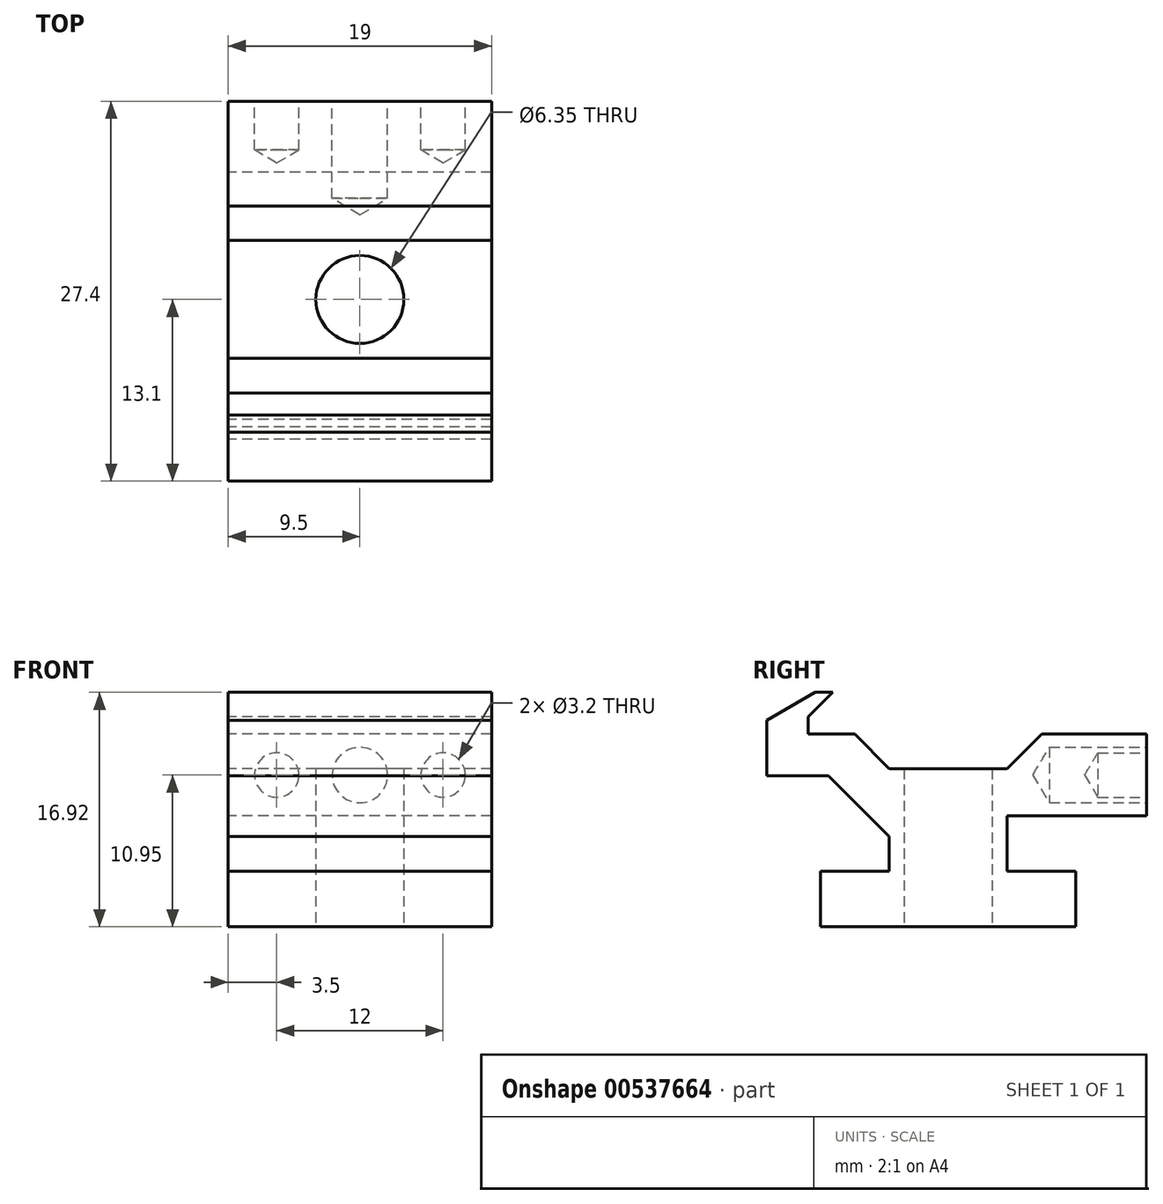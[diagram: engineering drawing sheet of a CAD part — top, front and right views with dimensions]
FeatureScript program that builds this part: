
annotation { "Feature Type Name" : "Feature", "Feature Type Description" : "" }
export const myFeature = defineFeature(function(context is Context, id is Id, definition is map)
    precondition{}
    {
        {
            var Q0;
            Q0=qCreatedBy(makeId("Right.planeOp"),FACE);
            var sketch = newSketch(context, id + "F0", { "sketchPlane" : qUnion([Q0])});
            skLineSegment(sketch, "E0.bottom", {"start": v(-9.2, -8.75) * mm, "end": v(9.2, -8.75) * mm});
            skLineSegment(sketch, "E0.top", {"start": v(-9.2, -4.75) * mm, "end": v(-4.25, -4.75) * mm});
            skLineSegment(sketch, "E0.left", {"start": v(-9.2, -8.75) * mm, "end": v(-9.2, -4.75) * mm});
            skLineSegment(sketch, "E0.right", {"start": v(9.2, -8.75) * mm, "end": v(9.2, -4.75) * mm});
            skLineSegment(sketch, "E1.top", {"start": v(-4.25, 2.65) * mm, "end": v(4.25, 2.65) * mm});
            skLineSegment(sketch, "E1.left", {"start": v(-4.25, -4.75) * mm, "end": v(-4.25, -2.25) * mm});
            skLineSegment(sketch, "E1.right", {"start": v(4.25, -4.75) * mm, "end": v(4.25, -0.75) * mm});
            skLineSegment(sketch, "E2", {"start": v(4.25, 2.65) * mm, "end": v(6.75, 5.15) * mm});
            skLineSegment(sketch, "E3", {"start": v(-4.25, 2.65) * mm, "end": v(-6.75, 5.15) * mm});
            skLineSegment(sketch, "E4", {"start": v(4.25, -0.75) * mm, "end": v(14.3, -0.75) * mm});
            skLineSegment(sketch, "E5", {"start": v(14.3, -0.75) * mm, "end": v(14.3, 5.15) * mm});
            skLineSegment(sketch, "E6", {"start": v(14.3, 5.15) * mm, "end": v(6.75, 5.15) * mm});
            skLineSegment(sketch, "E7.trimOffspring", {"start": v(4.25, -4.75) * mm, "end": v(9.2, -4.75) * mm});
            skLineSegment(sketch, "E8", {"start": v(-4.25, -2.25) * mm, "end": v(-8.65, 2.15) * mm});
            skLineSegment(sketch, "E9", {"start": v(-6.75, 5.15) * mm, "end": v(-10.1, 5.15) * mm});
            skLineSegment(sketch, "E10", {"start": v(-8.65, 2.15) * mm, "end": v(-13.1, 2.15) * mm});
            skLineSegment(sketch, "E11", {"start": v(-13.1, 2.15) * mm, "end": v(-13.1, 6.15) * mm});
            skLineSegment(sketch, "E12", {"start": v(-10.1, 5.15) * mm, "end": v(-10.1, 6.4) * mm});
            skLineSegment(sketch, "E13", {"start": v(-10.1, 6.4) * mm, "end": v(-8.33, 8.17) * mm});
            skLineSegment(sketch, "E14", {"start": v(-8.33, 8.17) * mm, "end": v(-9.58, 8.17) * mm});
            skLineSegment(sketch, "E15", {"start": v(-13.1, 6.15) * mm, "end": v(-9.58, 8.17) * mm});
            skSolve(sketch);
        }
        {
            var Q0;
            Q0 = qSketchRegion(id + "F0", true);
            extrude(context, id + "F1", {"entities" : qUnion([Q0]), "endBound" : BoundingType.SYMMETRIC, "depth" : 19 * mm, "offsetDistance" : 25 * mm});
        }
        {
            var Q0;
            Q0=makeQuery(id+"F1.opExtrude","SWEPT_FACE",FACE,{"disambiguationData":[OSD([sQuery(id+"F0.wireOp",EDGE,"E0.bottom")])]});
            var sketch = newSketch(context, id + "F2", { "sketchPlane" : qUnion([Q0])});
            skPoint(sketch, "E16", {"position": v(0, 0) * mm});
            skSolve(sketch);
        }
        {
            var Q0;
            Q0=sQuery(id+"F2.wireOp",VERTEX,"E16");
            var Q1;
            Q1=makeQuery(id+"F1.opExtrude","SWEPT_BODY",BODY,{"disambiguationData":[OSD([sQuery(id+"F0.wireOp",EDGE,"E0.bottom"),sQuery(id+"F0.wireOp",EDGE,"E0.top"),sQuery(id+"F0.wireOp",EDGE,"E0.left"),sQuery(id+"F0.wireOp",EDGE,"E0.right"),sQuery(id+"F0.wireOp",EDGE,"E1.top"),sQuery(id+"F0.wireOp",EDGE,"E1.left"),sQuery(id+"F0.wireOp",EDGE,"E1.right"),sQuery(id+"F0.wireOp",EDGE,"E2"),sQuery(id+"F0.wireOp",EDGE,"E3"),sQuery(id+"F0.wireOp",EDGE,"E4"),sQuery(id+"F0.wireOp",EDGE,"E5"),sQuery(id+"F0.wireOp",EDGE,"E6"),sQuery(id+"F0.wireOp",EDGE,"E7.trimOffspring"),sQuery(id+"F0.wireOp",EDGE,"E8"),sQuery(id+"F0.wireOp",EDGE,"E9"),sQuery(id+"F0.wireOp",EDGE,"E10"),sQuery(id+"F0.wireOp",EDGE,"E11"),sQuery(id+"F0.wireOp",EDGE,"E12"),sQuery(id+"F0.wireOp",EDGE,"E13"),sQuery(id+"F0.wireOp",EDGE,"E14"),sQuery(id+"F0.wireOp",EDGE,"E15")])]});
            hole(context, id + "F3", {"style" : HoleStyle.SIMPLE, "endStyle" : HoleEndStyle.THROUGH, "holeDiameter" : 6.35 * mm, "isTappedThrough" : true, "tappedDepth" : 12 * mm, "tapClearance" : 3, "locations" : qUnion([Q0]), "scope" : qUnion([Q1])});
        }
        {
            var Q0;
            Q0=makeQuery(id+"F1.opExtrude","SWEPT_FACE",FACE,{"disambiguationData":[OSD([sQuery(id+"F0.wireOp",EDGE,"E5")])]});
            var sketch = newSketch(context, id + "F4", { "sketchPlane" : qUnion([Q0])});
            skPoint(sketch, "E17", {"position": v(0, 2.2) * mm});
            skPoint(sketch, "E17.positionSnap0", {"position": v(-9.5, 2.2) * mm});
            skPoint(sketch, "E18", {"position": v(-6, 2.2) * mm});
            skPoint(sketch, "E19.MirrorP", {"position": v(6, 2.2) * mm});
            skSolve(sketch);
        }
        {
            var Q0;
            Q0=sQuery(id+"F4.wireOp",VERTEX,"E17");
            var Q1;
            Q1=makeQuery(id+"F1.opExtrude","SWEPT_BODY",BODY,{"disambiguationData":[OSD([sQuery(id+"F0.wireOp",EDGE,"E0.bottom"),sQuery(id+"F0.wireOp",EDGE,"E0.top"),sQuery(id+"F0.wireOp",EDGE,"E0.left"),sQuery(id+"F0.wireOp",EDGE,"E0.right"),sQuery(id+"F0.wireOp",EDGE,"E1.top"),sQuery(id+"F0.wireOp",EDGE,"E1.left"),sQuery(id+"F0.wireOp",EDGE,"E1.right"),sQuery(id+"F0.wireOp",EDGE,"E2"),sQuery(id+"F0.wireOp",EDGE,"E3"),sQuery(id+"F0.wireOp",EDGE,"E4"),sQuery(id+"F0.wireOp",EDGE,"E5"),sQuery(id+"F0.wireOp",EDGE,"E6"),sQuery(id+"F0.wireOp",EDGE,"E7.trimOffspring"),sQuery(id+"F0.wireOp",EDGE,"E8"),sQuery(id+"F0.wireOp",EDGE,"E9"),sQuery(id+"F0.wireOp",EDGE,"E10"),sQuery(id+"F0.wireOp",EDGE,"E11"),sQuery(id+"F0.wireOp",EDGE,"E12"),sQuery(id+"F0.wireOp",EDGE,"E13"),sQuery(id+"F0.wireOp",EDGE,"E14"),sQuery(id+"F0.wireOp",EDGE,"E15")])]});
            hole(context, id + "F5", {"style" : HoleStyle.SIMPLE, "endStyle" : HoleEndStyle.BLIND, "holeDiameter" : 4 * mm, "holeDepth" : 7 * mm, "isTappedThrough" : true, "tappedDepth" : 12 * mm, "tapClearance" : 3, "locations" : qUnion([Q0]), "scope" : qUnion([Q1])});
        }
        {
            var Q0;
            Q0=sQuery(id+"F4.wireOp",VERTEX,"E18");
            var Q1;
            Q1=sQuery(id+"F4.wireOp",VERTEX,"E19.MirrorP");
            var Q2;
            Q2=makeQuery(id+"F1.opExtrude","SWEPT_BODY",BODY,{"disambiguationData":[OSD([sQuery(id+"F0.wireOp",EDGE,"E0.bottom"),sQuery(id+"F0.wireOp",EDGE,"E0.top"),sQuery(id+"F0.wireOp",EDGE,"E0.left"),sQuery(id+"F0.wireOp",EDGE,"E0.right"),sQuery(id+"F0.wireOp",EDGE,"E1.top"),sQuery(id+"F0.wireOp",EDGE,"E1.left"),sQuery(id+"F0.wireOp",EDGE,"E1.right"),sQuery(id+"F0.wireOp",EDGE,"E2"),sQuery(id+"F0.wireOp",EDGE,"E3"),sQuery(id+"F0.wireOp",EDGE,"E4"),sQuery(id+"F0.wireOp",EDGE,"E5"),sQuery(id+"F0.wireOp",EDGE,"E6"),sQuery(id+"F0.wireOp",EDGE,"E7.trimOffspring"),sQuery(id+"F0.wireOp",EDGE,"E8"),sQuery(id+"F0.wireOp",EDGE,"E9"),sQuery(id+"F0.wireOp",EDGE,"E10"),sQuery(id+"F0.wireOp",EDGE,"E11"),sQuery(id+"F0.wireOp",EDGE,"E12"),sQuery(id+"F0.wireOp",EDGE,"E13"),sQuery(id+"F0.wireOp",EDGE,"E14"),sQuery(id+"F0.wireOp",EDGE,"E15")])]});
            hole(context, id + "F6", {"style" : HoleStyle.SIMPLE, "endStyle" : HoleEndStyle.BLIND, "holeDiameter" : 3.2 * mm, "holeDepth" : 3.5 * mm, "isTappedThrough" : true, "tappedDepth" : 12 * mm, "tapClearance" : 3, "locations" : qUnion([Q0, Q1]), "scope" : qUnion([Q2])});
        }
    });
